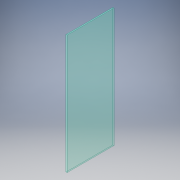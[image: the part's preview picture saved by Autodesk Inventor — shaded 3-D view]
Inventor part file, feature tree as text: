
AUTODESK INVENTOR PART (.ipt)
format: ipt  version: 2019 (Build 230136000, 136)  size: 94,208 bytes
history: native  units: in
note: dims shown in document units (in); Inventor stores cm internally (conversion verified against a paired STEP export)
features: extrude x1, sketch x1
ambient origin geometry x8: Origin, YZ Plane, XZ Plane, XY Plane, X Axis, Y Axis, Z Axis, Center Point
bodies: Solid1 (feature_tree)
feature tree (2):
  extrude  "Extrusion1"  Depth=3.2542in
  sketch  "Sketch1"  dims[d0=0.0787in d1=3.2542in d2=8.2677in d3=0.0in]
